# Revit family: REC-PAA2005010R
name_source: partatom
category: Structural Connections
units: mm (PartAtom-declared; Revit-internal decimal feet)

## family parameters
Cut with Voids When Loaded = Yes
Enable Cutting in Views = Yes
Host = Face
Material for Model Behavior = Steel
Shared = No

## types (1)
- PAA2005010R
    Classification.Uniclass.Pr.Description = Carbon steel anchor plates
    Classification.Uniclass.Pr.Number = Pr_20_29_03_10
    Cost = 0 $
    Creado por: = Deliprogal SL
    Default Elevation = 0 mm  [stored 0 ft]
    Description = Non-slip angle plate 200x50x80x80x10 mm with 2 slotted holes 15x9 mm.
    Description_ESP = Pletina angular antideslizante 200x50x80x10 mm 2 ranuras 15x9 mm.
    Export Type to IFC As = IfcElementAssembly
    Fecha Ultima Revision: = 01/03/2024
    Fecha de Creacion: = 01/03/2024
    IFCExportAs = IfcElementAssembly
    IFCExportType = Carbon steel anchor plates
    Keynote = Supporting bracket system for GRC concrete panels
GRC concrete panels STUD FRAME type.
    Keynote_ESP = Sistema de ménsula portante para paneles de hormigón GRC tipo STUD FRAME.
    Manufacturer = RECENSE
    Model = PAA2005010R
    Type IFC Predefined Type = Brackets
    URL = https://recense.com
    Visible = Yes

note: [stored X ft] marks values corroborated as IEEE doubles in the binary element streams (Revit-internal decimal feet)

## geometry (parser evidence)
native form markers: Sweep x1
no freeform markers — native parametric forms only
